# Revit family: Steni - Profile - Horizontal Joint HFP 7-30
name_source: partatom
category: Generic Models
revit_build: Autodesk Revit Architecture 2016 (Build: 20151007_0715(x64)
units: mm (PartAtom-declared; Revit-internal decimal feet)

## family parameters
Always vertical = Yes
Can host rebar = No
Cut with Voids When Loaded = No
Part Type = Normal
Room Calculation Point = No
Round Connector Dimension = Use Diameter
Shared = No
Work Plane-Based = No

## types (3) — shared parameters
DepthBig = 5 mm  [stored 0.0164042 ft]
DepthSmall = 1 mm  [stored 0.00328084 ft]
Description = Aluminium profile for Steni facade systems
Manufacturer = www.steni.com
Model = HFP 7-30
Product family = Steni Profiles
URL = http://bimobject.com
zero-valued in all types: Width

## per-type parameters (varying)
| type | Material main |
| Anodized 15µ | Steni Aluminium Profile Anodized |
| S 0502-Y White | Steni Aluminium Profile White S0502-Y |
| RAL 9005 Black | Steni Aluminium Profile Black RAL9005 |

note: [stored X ft] marks values corroborated as IEEE doubles in the binary element streams (Revit-internal decimal feet)

## geometry (parser evidence)
native form markers: Blend x4, Sweep x3
no freeform markers — native parametric forms only
